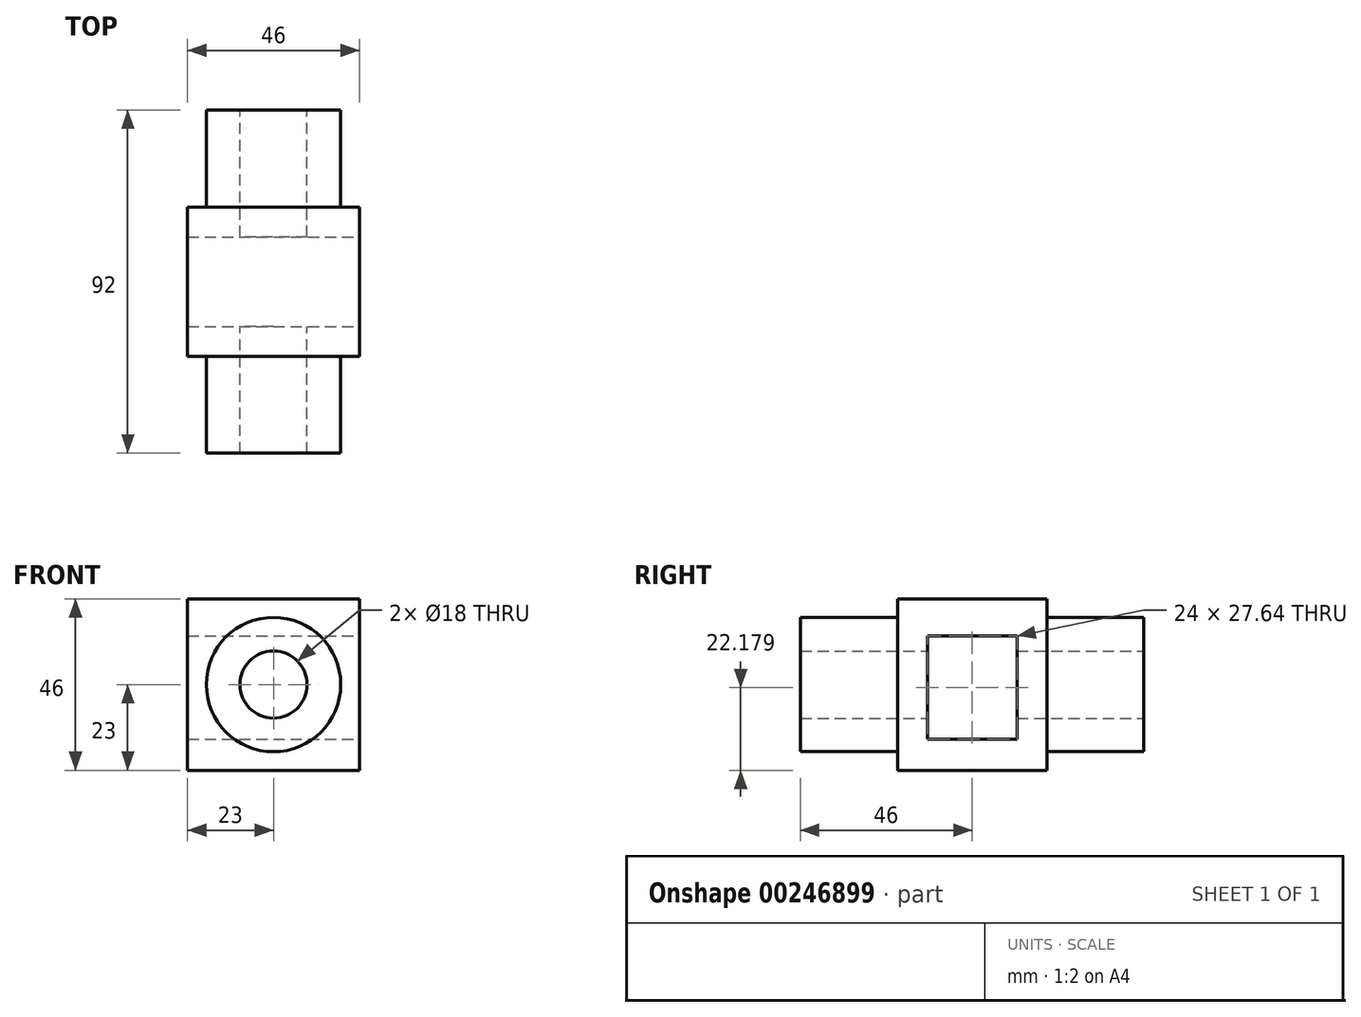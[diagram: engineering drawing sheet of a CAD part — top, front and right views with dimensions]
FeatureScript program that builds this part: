
annotation { "Feature Type Name" : "Feature", "Feature Type Description" : "" }
export const myFeature = defineFeature(function(context is Context, id is Id, definition is map)
    precondition{}
    {
        {
            var Q0;
            Q0=qCreatedBy(makeId("Top.planeOp"),FACE);
            var sketch = newSketch(context, id + "F0", { "sketchPlane" : qUnion([Q0])});
            skLineSegment(sketch, "E0.bottom", {"start": v(0, 0) * mm, "end": v(46, 0) * mm});
            skLineSegment(sketch, "E0.top", {"start": v(0, -40) * mm, "end": v(46, -40) * mm});
            skLineSegment(sketch, "E0.left", {"start": v(0, 0) * mm, "end": v(0, -40) * mm});
            skLineSegment(sketch, "E0.right", {"start": v(46, 0) * mm, "end": v(46, -40) * mm});
            skSolve(sketch);
        }
        {
            var Q0;
            Q0=makeQuery(id+"F0.imprint","IMPRINT",FACE,{"disambiguationData":[TD([[makeQuery(id+"F0.imprint","IMPRINT",EDGE,{"derivedFrom":sQuery(id+"F0.wireOp",EDGE,"E0.bottom")}),-1.0]])]});
            extrude(context, id + "F1", {"entities" : qUnion([Q0]), "depth" : 46 * mm});
        }
        {
            var Q0;
            Q0=makeQuery(id+"F1.opExtrude","SWEPT_FACE",FACE,{"disambiguationData":[OSD([sQuery(id+"F0.wireOp",EDGE,"E0.right")])]});
            var sketch = newSketch(context, id + "F2", { "sketchPlane" : qUnion([Q0])});
            skLineSegment(sketch, "E1.bottom", {"start": v(-40, 46) * mm, "end": v(0, 46) * mm});
            skLineSegment(sketch, "E1.top", {"start": v(-40, 36) * mm, "end": v(0, 36) * mm});
            skLineSegment(sketch, "E1.left", {"start": v(-40, 46) * mm, "end": v(-40, 36) * mm});
            skLineSegment(sketch, "E1.right", {"start": v(0, 46) * mm, "end": v(0, 36) * mm});
            skLineSegment(sketch, "E2.bottom", {"start": v(-40, 46) * mm, "end": v(-32, 46) * mm});
            skLineSegment(sketch, "E2.top", {"start": v(-40, 0) * mm, "end": v(-32, 0) * mm});
            skLineSegment(sketch, "E2.left", {"start": v(-40, 46) * mm, "end": v(-40, 0) * mm});
            skLineSegment(sketch, "E2.right", {"start": v(-32, 46) * mm, "end": v(-32, 0) * mm});
            skLineSegment(sketch, "E3.bottom", {"start": v(0, 0) * mm, "end": v(-40, 0) * mm});
            skLineSegment(sketch, "E3.top", {"start": v(0, 8.36) * mm, "end": v(-40, 8.36) * mm});
            skLineSegment(sketch, "E3.left", {"start": v(0, 0) * mm, "end": v(0, 8.36) * mm});
            skLineSegment(sketch, "E3.right", {"start": v(-40, 0) * mm, "end": v(-40, 8.36) * mm});
            skLineSegment(sketch, "E4.bottom", {"start": v(0, 0) * mm, "end": v(-8, 0) * mm});
            skLineSegment(sketch, "E4.top", {"start": v(0, 46) * mm, "end": v(-8, 46) * mm});
            skLineSegment(sketch, "E4.left", {"start": v(0, 0) * mm, "end": v(0, 46) * mm});
            skLineSegment(sketch, "E4.right", {"start": v(-8, 0) * mm, "end": v(-8, 46) * mm});
            skSolve(sketch);
        }
        {
            var Q0;
            {var subQ0=sQuery(id+"F2.wireOp",EDGE,"E2.right");var subQ1=sQuery(id+"F2.wireOp",EDGE,"E1.top");var subQ2=makeQuery(id+"F2.imprint","INTERSECT",VERTEX,{"derivedFrom":[subQ1,subQ0]});Q0=makeQuery(id+"F2.imprint","IMPRINT",FACE,{"disambiguationData":[TD([[makeQuery(id+"F2.imprint","IMPRINT",EDGE,{"disambiguationData":[TD([[subQ2,-1.0]])],"derivedFrom":subQ1}),-1.0]])]});}
            extrude(context, id + "F3", {"entities" : qUnion([Q0]), "operationType" : NewBodyOperationType.REMOVE, "oppositeDirection" : true, "depth" : 46 * mm});
        }
        {
            var Q0;
            Q0=makeQuery(id+"F1.opExtrude","SWEPT_FACE",FACE,{"disambiguationData":[OSD([sQuery(id+"F0.wireOp",EDGE,"E0.bottom")])]});
            var sketch = newSketch(context, id + "F4", { "sketchPlane" : qUnion([Q0])});
            skCircle(sketch, "E5", {"center": v(-23, 23) * mm, "radius": 9 * mm});
            skPoint(sketch, "E5.centerSnap0", {"position": v(-23, 46) * mm});
            skPoint(sketch, "E5.centerSnap1", {"position": v(-46, 23) * mm});
            skSolve(sketch);
        }
        {
            var Q0;
            Q0=makeQuery(id+"F1.opExtrude","SWEPT_FACE",FACE,{"disambiguationData":[OSD([sQuery(id+"F0.wireOp",EDGE,"E0.bottom")])]});
            var sketch = newSketch(context, id + "F5", { "sketchPlane" : qUnion([Q0])});
            skCircle(sketch, "E6", {"center": v(-23, 23) * mm, "radius": 18 * mm});
            skPoint(sketch, "E6.centerSnap0", {"position": v(-46, 23) * mm});
            skPoint(sketch, "E6.centerSnap1", {"position": v(-23, 46) * mm});
            skSolve(sketch);
        }
        {
            var Q0;
            Q0=makeQuery(id+"F4.imprint","IMPRINT",FACE,{"disambiguationData":[TD([[makeQuery(id+"F4.imprint","IMPRINT",EDGE,{"derivedFrom":sQuery(id+"F4.wireOp",EDGE,"E5")}),1.0]])]});
            extrude(context, id + "F6", {"entities" : qUnion([Q0]), "operationType" : NewBodyOperationType.REMOVE, "oppositeDirection" : true, "depth" : 46 * mm});
        }
        {
            var Q0;
            Q0 = qSketchRegion(id + "F5", true);
            extrude(context, id + "F7", {"entities" : qUnion([Q0]), "operationType" : NewBodyOperationType.ADD, "depth" : 26 * mm});
        }
        {
            var Q0;
            Q0=makeQuery(id+"F7.opExtrude","CAP_FACE",FACE,{"disambiguationData":[OSD([sQuery(id+"F5.wireOp",EDGE,"E6")])],"isStart":false});
            var sketch = newSketch(context, id + "F8", { "sketchPlane" : qUnion([Q0])});
            skCircle(sketch, "E7", {"center": v(-23, 23) * mm, "radius": 9 * mm});
            skSolve(sketch);
        }
        {
            var Q0;
            Q0=makeQuery(id+"F8.imprint","IMPRINT",FACE,{"disambiguationData":[TD([[makeQuery(id+"F8.imprint","IMPRINT",EDGE,{"derivedFrom":sQuery(id+"F8.wireOp",EDGE,"E7")}),1.0]])]});
            extrude(context, id + "F9", {"entities" : qUnion([Q0]), "operationType" : NewBodyOperationType.REMOVE, "oppositeDirection" : true, "depth" : 26 * mm});
        }
        {
            var Q0;
            Q0=makeQuery(id+"F1.opExtrude","SWEPT_FACE",FACE,{"disambiguationData":[OSD([sQuery(id+"F0.wireOp",EDGE,"E0.top")])]});
            var sketch = newSketch(context, id + "F10", { "sketchPlane" : qUnion([Q0])});
            skCircle(sketch, "E8", {"center": v(23, 23) * mm, "radius": 18 * mm});
            skSolve(sketch);
        }
        {
            var Q0;
            Q0=makeQuery(id+"F10.imprint","IMPRINT",FACE,{"disambiguationData":[TD([[makeQuery(id+"F10.imprint","IMPRINT",EDGE,{"derivedFrom":sQuery(id+"F10.wireOp",EDGE,"E8")}),1.0]])]});
            extrude(context, id + "F11", {"entities" : qUnion([Q0]), "operationType" : NewBodyOperationType.ADD, "depth" : 26 * mm});
        }
    });
